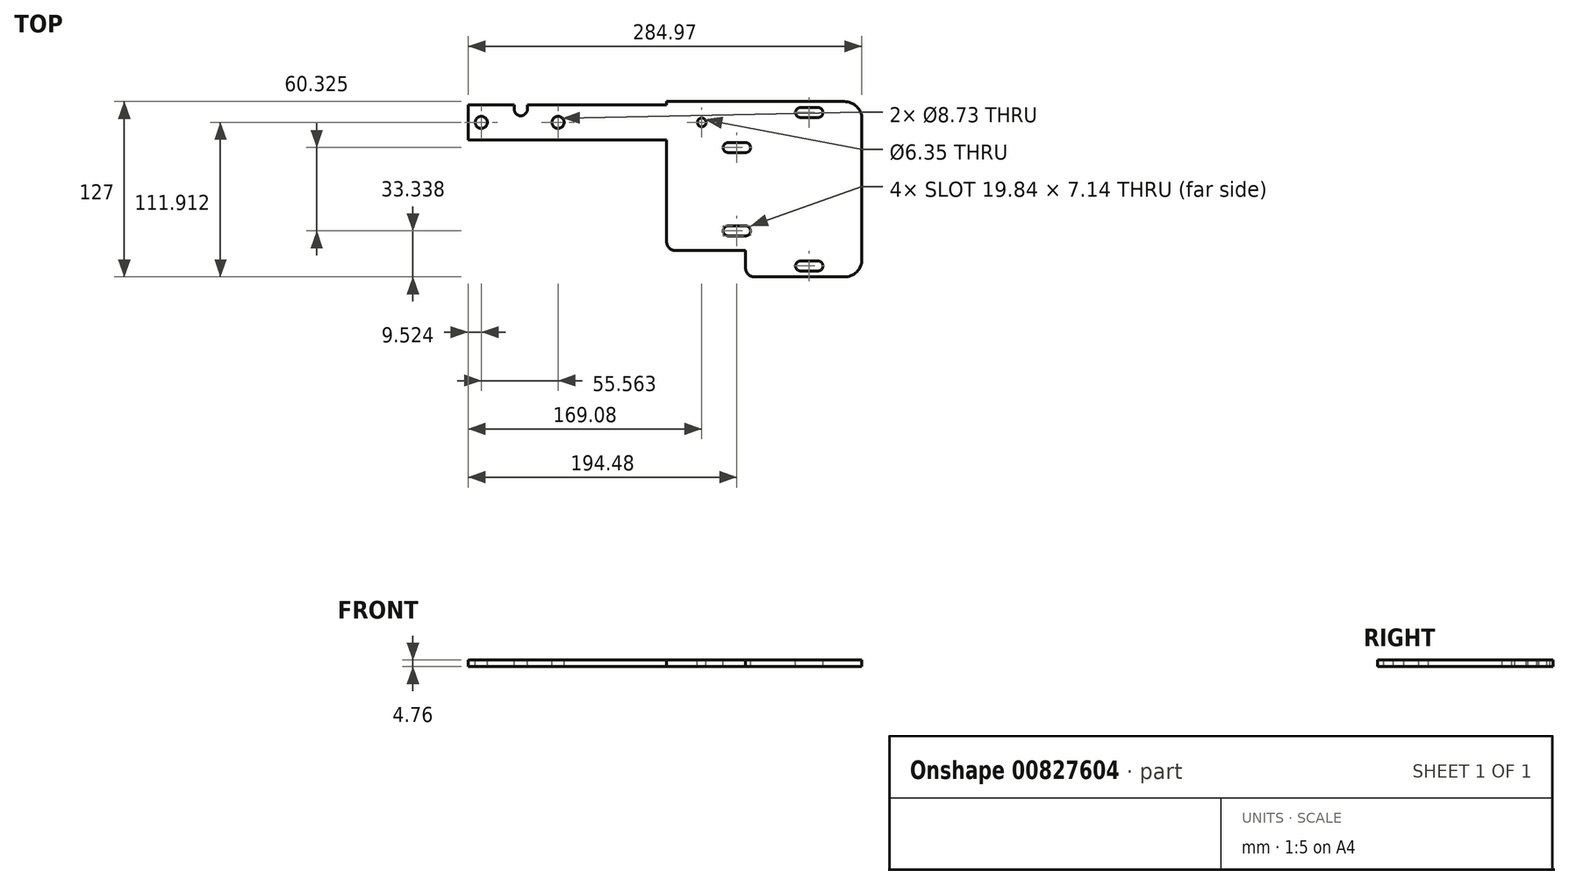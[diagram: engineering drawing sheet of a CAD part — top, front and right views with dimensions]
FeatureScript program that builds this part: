
annotation { "Feature Type Name" : "Feature", "Feature Type Description" : "" }
export const myFeature = defineFeature(function(context is Context, id is Id, definition is map)
    precondition{}
    {
        {
            var Q0;
            Q0=qCreatedBy(makeId("Top.planeOp"),FACE);
            var sketch = newSketch(context, id + "F0", { "sketchPlane" : qUnion([Q0])});
            skLineSegment(sketch, "E0", {"start": v(0, 0) * mm, "end": v(0, -2.39) * mm});
            skLineSegment(sketch, "E1", {"start": v(63.5, -127) * mm, "end": v(128.59, -127) * mm});
            skLineSegment(sketch, "E2", {"start": v(6.35, -107.95) * mm, "end": v(57.15, -107.95) * mm});
            skLineSegment(sketch, "E3", {"start": v(57.15, -107.95) * mm, "end": v(57.15, -120.65) * mm});
            skPoint(sketch, "E4.visualSharp", {"position": v(0, -107.95) * mm});
            skArc(sketch, "E4.filletArc", {"start": v(0, -101.6) * mm, "mid": v(1.86, -106.1) * mm, "end": v(6.35, -107.95) * mm});
            skPoint(sketch, "E5.visualSharp", {"position": v(57.15, -127) * mm});
            skArc(sketch, "E5.filletArc", {"start": v(57.15, -120.65) * mm, "mid": v(59, -125.14) * mm, "end": v(63.5, -127) * mm});
            skLineSegment(sketch, "E6", {"start": v(0, 0) * mm, "end": v(128.59, 0) * mm});
            skLineSegment(sketch, "E7", {"start": v(141.29, -12.7) * mm, "end": v(141.29, -114.3) * mm});
            skPoint(sketch, "E8.visualSharp", {"position": v(141.29, -127) * mm});
            skArc(sketch, "E8.filletArc", {"start": v(128.59, -127) * mm, "mid": v(137.57, -123.28) * mm, "end": v(141.29, -114.3) * mm});
            skPoint(sketch, "E9.visualSharp", {"position": v(141.29, 0) * mm});
            skArc(sketch, "E9.filletArc", {"start": v(141.29, -12.7) * mm, "mid": v(137.57, -3.72) * mm, "end": v(128.59, 0) * mm});
            skArc(sketch, "E10", {"start": v(57.15, -36.9) * mm, "mid": v(60.72, -33.34) * mm, "end": v(57.15, -29.77) * mm});
            skArc(sketch, "E11", {"start": v(44.45, -29.77) * mm, "mid": v(40.88, -33.34) * mm, "end": v(44.45, -36.9) * mm});
            skLineSegment(sketch, "E12", {"start": v(44.45, -29.77) * mm, "end": v(57.15, -29.77) * mm});
            skLineSegment(sketch, "E13", {"start": v(57.15, -36.9) * mm, "end": v(44.45, -36.9) * mm});
            skPoint(sketch, "E14", {"position": v(141.29, -63.5) * mm});
            skArc(sketch, "E15", {"start": v(57.15, -97.23) * mm, "mid": v(60.72, -93.66) * mm, "end": v(57.15, -90.1) * mm});
            skArc(sketch, "E16", {"start": v(44.45, -90.1) * mm, "mid": v(40.88, -93.66) * mm, "end": v(44.45, -97.23) * mm});
            skLineSegment(sketch, "E17", {"start": v(44.45, -90.1) * mm, "end": v(57.15, -90.1) * mm});
            skLineSegment(sketch, "E18", {"start": v(57.15, -97.23) * mm, "end": v(44.45, -97.23) * mm});
            skArc(sketch, "E19", {"start": v(109.54, -11.5) * mm, "mid": v(113.1, -7.94) * mm, "end": v(109.54, -4.37) * mm});
            skArc(sketch, "E20", {"start": v(96.84, -4.37) * mm, "mid": v(93.27, -7.94) * mm, "end": v(96.84, -11.5) * mm});
            skLineSegment(sketch, "E21", {"start": v(96.84, -4.37) * mm, "end": v(109.54, -4.37) * mm});
            skLineSegment(sketch, "E22", {"start": v(109.54, -11.5) * mm, "end": v(96.84, -11.5) * mm});
            skArc(sketch, "E23", {"start": v(109.54, -122.63) * mm, "mid": v(113.1, -119.06) * mm, "end": v(109.54, -115.5) * mm});
            skArc(sketch, "E24", {"start": v(96.84, -115.5) * mm, "mid": v(93.27, -119.06) * mm, "end": v(96.84, -122.63) * mm});
            skLineSegment(sketch, "E25", {"start": v(96.84, -115.5) * mm, "end": v(109.54, -115.5) * mm});
            skLineSegment(sketch, "E26", {"start": v(109.54, -122.63) * mm, "end": v(96.84, -122.63) * mm});
            skLineSegment(sketch, "E27", {"start": v(-143.68, -2.39) * mm, "end": v(-143.68, -27.79) * mm});
            skLineSegment(sketch, "E28", {"start": v(-143.68, -27.79) * mm, "end": v(0, -27.79) * mm});
            skLineSegment(sketch, "E29.trimOffspring", {"start": v(0, -27.79) * mm, "end": v(0, -101.6) * mm});
            skLineSegment(sketch, "E30.trimOffspring", {"start": v(0, -2.39) * mm, "end": v(-100.82, -2.39) * mm});
            skCircle(sketch, "E31.MirrorC", {"center": v(-78.6, -15.09) * mm, "radius": 4.37 * mm});
            skCircle(sketch, "E32.MirrorC", {"center": v(-134.16, -15.09) * mm, "radius": 4.37 * mm});
            skArc(sketch, "E33.MirrorCS", {"start": v(-100.82, -5.56) * mm, "mid": v(-105.58, -10.33) * mm, "end": v(-110.34, -5.56) * mm});
            skLineSegment(sketch, "E34.MirrorCS", {"start": v(-110.34, -5.56) * mm, "end": v(-110.34, -2.39) * mm});
            skLineSegment(sketch, "E35.MirrorCS", {"start": v(-100.82, -5.56) * mm, "end": v(-100.82, -2.39) * mm});
            skLineSegment(sketch, "E36.trimOffspring", {"start": v(-110.34, -2.39) * mm, "end": v(-143.68, -2.39) * mm});
            skCircle(sketch, "E37", {"center": v(25.4, -15.09) * mm, "radius": 3.18 * mm});
            skSolve(sketch);
        }
        {
            var Q0;
            Q0 = qSketchRegion(id + "F0", true);
            extrude(context, id + "F1", {"entities" : qUnion([Q0]), "oppositeDirection" : true, "depth" : 4.76 * mm, "offsetDistance" : 25.4 * mm});
        }
    });
